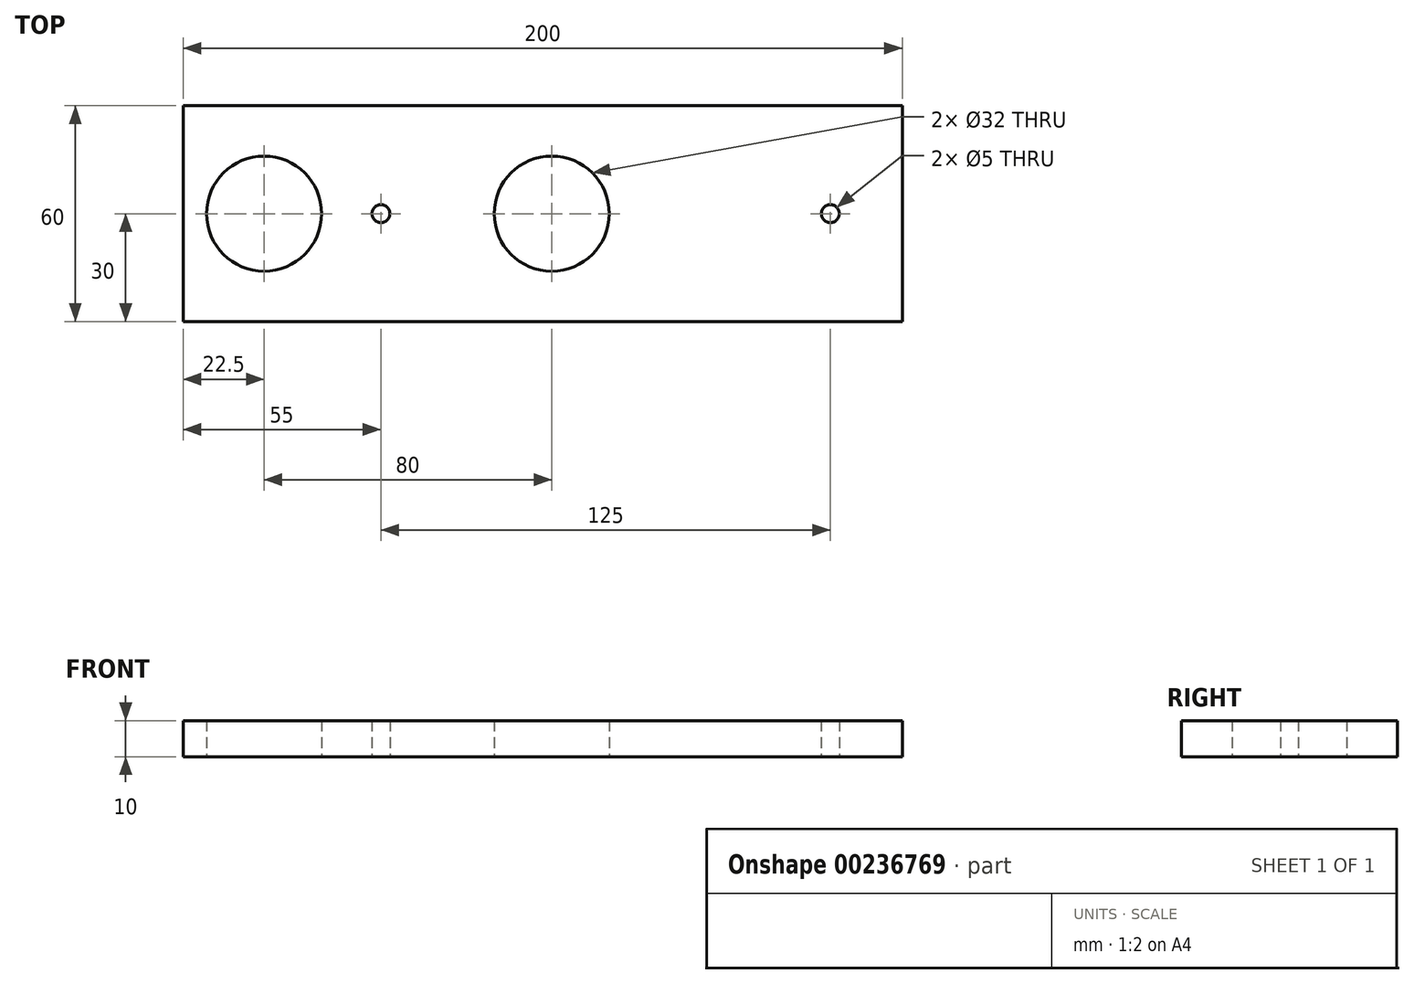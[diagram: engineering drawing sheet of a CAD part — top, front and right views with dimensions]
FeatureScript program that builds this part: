
annotation { "Feature Type Name" : "Feature", "Feature Type Description" : "" }
export const myFeature = defineFeature(function(context is Context, id is Id, definition is map)
    precondition{}
    {
        {
            var Q0;
            Q0=qCreatedBy(makeId("Top.planeOp"),FACE);
            var sketch = newSketch(context, id + "F0", { "sketchPlane" : qUnion([Q0])});
            skLineSegment(sketch, "E0.bottom", {"start": v(0, 0) * mm, "end": v(200, 0) * mm});
            skLineSegment(sketch, "E0.top", {"start": v(0, 60) * mm, "end": v(200, 60) * mm});
            skLineSegment(sketch, "E0.left", {"start": v(0, 0) * mm, "end": v(0, 60) * mm});
            skLineSegment(sketch, "E0.right", {"start": v(200, 0) * mm, "end": v(200, 60) * mm});
            skSolve(sketch);
        }
        {
            var Q0;
            Q0=makeQuery(id+"F0.imprint","IMPRINT",FACE,{"disambiguationData":[TD([[makeQuery(id+"F0.imprint","IMPRINT",EDGE,{"derivedFrom":sQuery(id+"F0.wireOp",EDGE,"E0.bottom")}),1.0]])]});
            extrude(context, id + "F1", {"entities" : qUnion([Q0]), "depth" : 10 * mm, "offsetDistance" : 25 * mm});
        }
        {
            var Q0;
            Q0=makeQuery(id+"F1.opExtrude","CAP_FACE",FACE,{"disambiguationData":[OSD([sQuery(id+"F0.wireOp",EDGE,"E0.bottom"),sQuery(id+"F0.wireOp",EDGE,"E0.top"),sQuery(id+"F0.wireOp",EDGE,"E0.left"),sQuery(id+"F0.wireOp",EDGE,"E0.right")])],"isStart":false});
            var sketch = newSketch(context, id + "F2", { "sketchPlane" : qUnion([Q0])});
            skPoint(sketch, "E1", {"position": v(22.5, 30) * mm});
            skPoint(sketch, "E2", {"position": v(102.5, 30) * mm});
            skPoint(sketch, "E3", {"position": v(180, 30) * mm});
            skPoint(sketch, "E4", {"position": v(55, 30) * mm});
            skSolve(sketch);
        }
        {
            var Q0;
            Q0=sQuery(id+"F2.wireOp",VERTEX,"E2");
            var Q1;
            Q1=sQuery(id+"F2.wireOp",VERTEX,"E1");
            var Q2;
            Q2=makeQuery(id+"F1.opExtrude","SWEPT_BODY",BODY,{"disambiguationData":[OSD([sQuery(id+"F0.wireOp",EDGE,"E0.bottom"),sQuery(id+"F0.wireOp",EDGE,"E0.top"),sQuery(id+"F0.wireOp",EDGE,"E0.left"),sQuery(id+"F0.wireOp",EDGE,"E0.right")])]});
            hole(context, id + "F3", {"style" : HoleStyle.SIMPLE, "endStyle" : HoleEndStyle.THROUGH, "holeDiameter" : 32 * mm, "majorDiameter" : 5 * mm, "isTappedThrough" : true, "tappedDepth" : 31.25 * mm, "tapClearance" : 3, "startFromSketch" : true, "locations" : qUnion([Q0, Q1]), "scope" : qUnion([Q2])});
        }
        {
            var Q0;
            Q0=makeQuery(id+"F1.opExtrude","CAP_FACE",FACE,{"disambiguationData":[OSD([sQuery(id+"F0.wireOp",EDGE,"E0.bottom"),sQuery(id+"F0.wireOp",EDGE,"E0.top"),sQuery(id+"F0.wireOp",EDGE,"E0.left"),sQuery(id+"F0.wireOp",EDGE,"E0.right")])],"isStart":false});
            var sketch = newSketch(context, id + "F4", { "sketchPlane" : qUnion([Q0])});
            skPoint(sketch, "E5", {"position": v(55, 30) * mm});
            skPoint(sketch, "E5.positionSnap0", {"position": v(0, 30) * mm});
            skPoint(sketch, "E6", {"position": v(180, 30) * mm});
            skSolve(sketch);
        }
        {
            var Q0;
            Q0=sQuery(id+"F4.wireOp",VERTEX,"E5");
            var Q1;
            Q1=sQuery(id+"F4.wireOp",VERTEX,"E6");
            var Q2;
            Q2=makeQuery(id+"F1.opExtrude","SWEPT_BODY",BODY,{"disambiguationData":[OSD([sQuery(id+"F0.wireOp",EDGE,"E0.bottom"),sQuery(id+"F0.wireOp",EDGE,"E0.top"),sQuery(id+"F0.wireOp",EDGE,"E0.left"),sQuery(id+"F0.wireOp",EDGE,"E0.right")])]});
            hole(context, id + "F5", {"style" : HoleStyle.SIMPLE, "endStyle" : HoleEndStyle.THROUGH, "holeDiameter" : 5 * mm, "majorDiameter" : 5 * mm, "isTappedThrough" : true, "tappedDepth" : 31.25 * mm, "tapClearance" : 3, "startFromSketch" : true, "locations" : qUnion([Q0, Q1]), "scope" : qUnion([Q2])});
        }
    });
